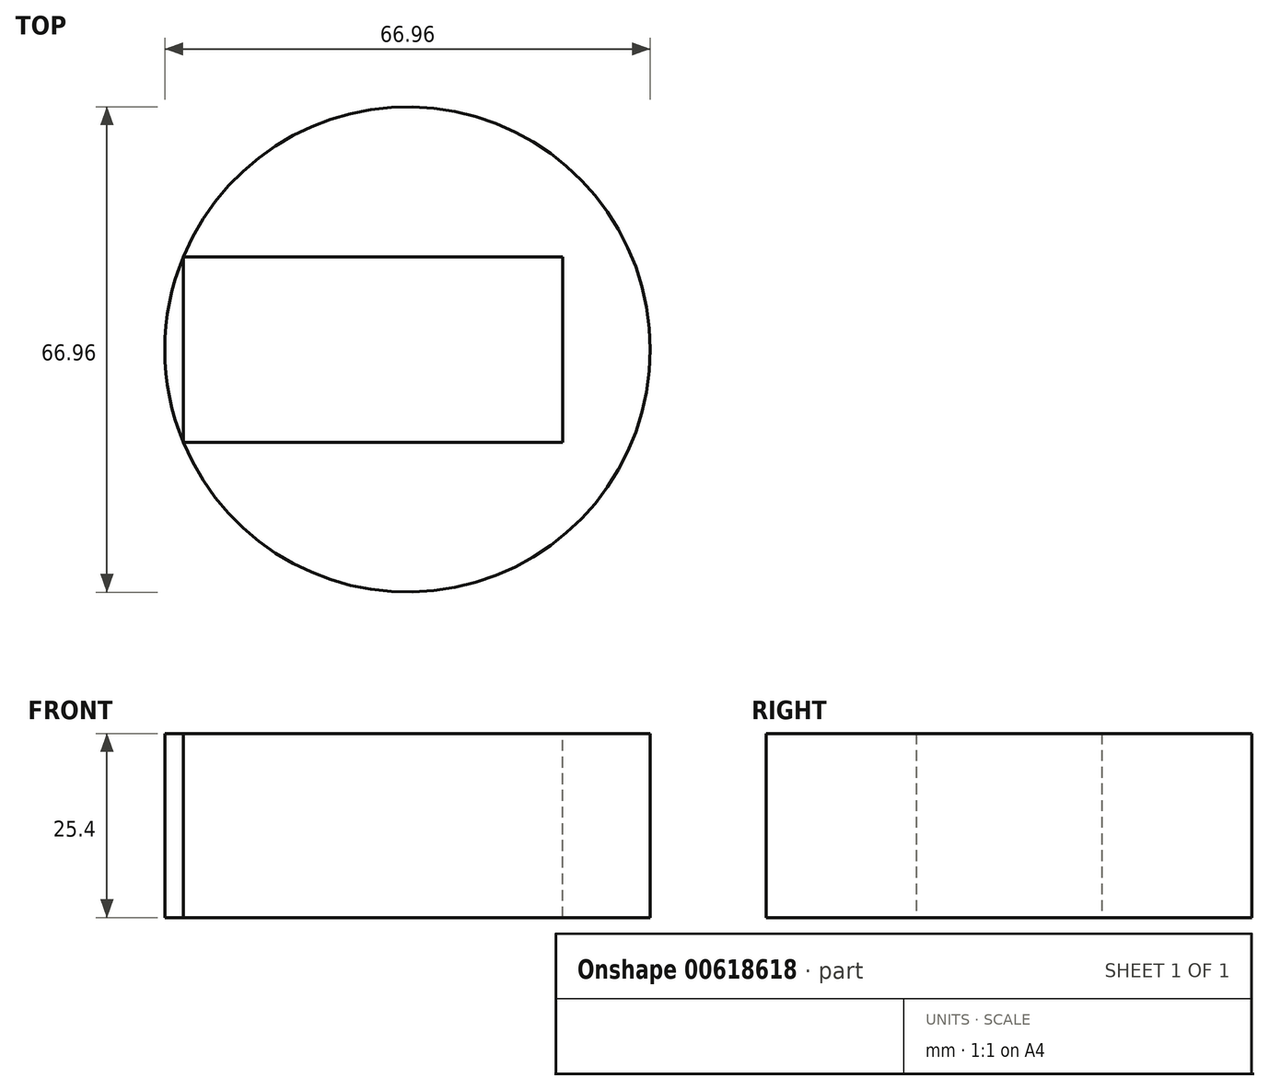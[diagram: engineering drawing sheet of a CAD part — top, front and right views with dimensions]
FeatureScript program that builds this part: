
annotation { "Feature Type Name" : "Feature", "Feature Type Description" : "" }
export const myFeature = defineFeature(function(context is Context, id is Id, definition is map)
    precondition{}
    {
        {
            var Q0;
            Q0=qCreatedBy(makeId("Top.planeOp"),FACE);
            var sketch = newSketch(context, id + "F0", { "sketchPlane" : qUnion([Q0])});
            skCircle(sketch, "E0", {"center": v(0, 0) * mm, "radius": 33.48 * mm});
            skSolve(sketch);
        }
        {
            var Q0;
            Q0 = qSketchRegion(id + "F0", true);
            extrude(context, id + "F1", {"entities" : qUnion([Q0]), "depth" : 25.4 * mm, "offsetDistance" : 25.4 * mm});
        }
        {
            var Q0;
            Q0=makeQuery(id+"F1.opExtrude","CAP_FACE",FACE,{"disambiguationData":[OSD([sQuery(id+"F0.wireOp",EDGE,"E0")])],"isStart":false});
            var sketch = newSketch(context, id + "F2", { "sketchPlane" : qUnion([Q0])});
            skLineSegment(sketch, "E1.bottom", {"start": v(-30.93, -12.8) * mm, "end": v(21.4, -12.8) * mm});
            skLineSegment(sketch, "E1.top", {"start": v(-30.93, 12.8) * mm, "end": v(21.4, 12.8) * mm});
            skLineSegment(sketch, "E1.left", {"start": v(-30.93, -12.8) * mm, "end": v(-30.93, 12.8) * mm});
            skLineSegment(sketch, "E1.right", {"start": v(21.4, -12.8) * mm, "end": v(21.4, 12.8) * mm});
            skSolve(sketch);
        }
        {
            var Q0;
            Q0 = qSketchRegion(id + "F2", true);
            extrude(context, id + "F3", {"entities" : qUnion([Q0]), "operationType" : NewBodyOperationType.REMOVE, "oppositeDirection" : true, "depth" : 37.85 * mm, "offsetDistance" : 25.4 * mm});
        }
    });
